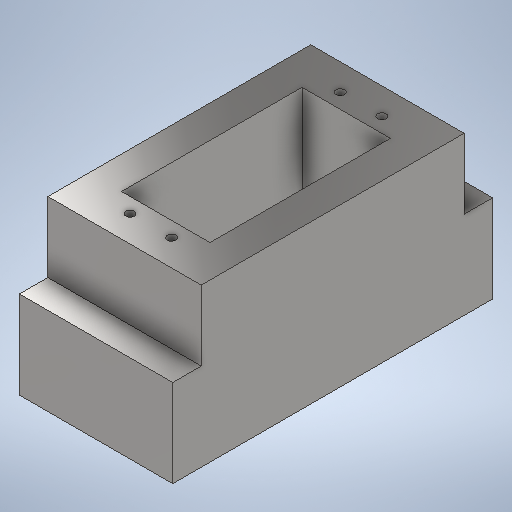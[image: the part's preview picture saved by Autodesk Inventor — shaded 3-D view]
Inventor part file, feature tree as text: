
AUTODESK INVENTOR PART (.ipt)
format: ipt  version: 2025.1 (Build 291241000, 241)  size: 288,768 bytes
history: native  units: mm
features: sketch x6, extrude x5, hole x1
ambient origin geometry x8: Origin, YZ Plane, XZ Plane, XY Plane, X Axis, Y Axis, Z Axis, Center Point
bodies: Solid1 (feature_tree)
feature tree (12):
  extrude  "Extrusion1"  Depth=73.0mm
  extrude  "Extrusion2"  TaperAngle=0.0deg  [1 undecoded]
  extrude  "Extrusion4"  Depth=50.0mm
  extrude  "Extrusion8"  Depth=6.0mm
  extrude  "Extrusion9"  Depth=6.0mm
  hole  "Hole1"  [1 undecoded]
  sketch  "Sketch1"  dims[d0=35.0mm d1=73.0mm]
  sketch  "Sketch2"  dims[d2=6.0mm d3=0.0mm]
  sketch  "Sketch4"  dims[d4=29.0mm d5=50.0mm]
  sketch  "Sketch9"  dims[d9=14.0mm d10=0.0mm d15=6.0mm]
  sketch  "Sketch10"  dims[d16=6.0mm d19=12.0mm]
  sketch  "Sketch12"  dims[d20=30.0mm d21=48.015mm d22=2.8mm d23=4.5mm d24=4.007mm d25=2.8mm d26=6.5mm d27=15.507mm d28=0.0mm d29=0.0mm d45=20.2mm d46=41.2mm d47=16.0mm d48=10.0mm d49=0.0mm d50=0.0mm d51=35.0mm d52=60.0mm d53=0.0mm d54=0.0mm d55=9.5mm d56=48.0mm d57=2.0mm d58=6.0mm d59=4.0mm d60=2.0mm d61=90.0deg d62=15.0mm d63=0.0mm]
note: 2 required parameter values undecoded (feature->parameter linkage not recoverable at this tier; creation-order binding heuristic only, values carry confidence <= 0.55)
